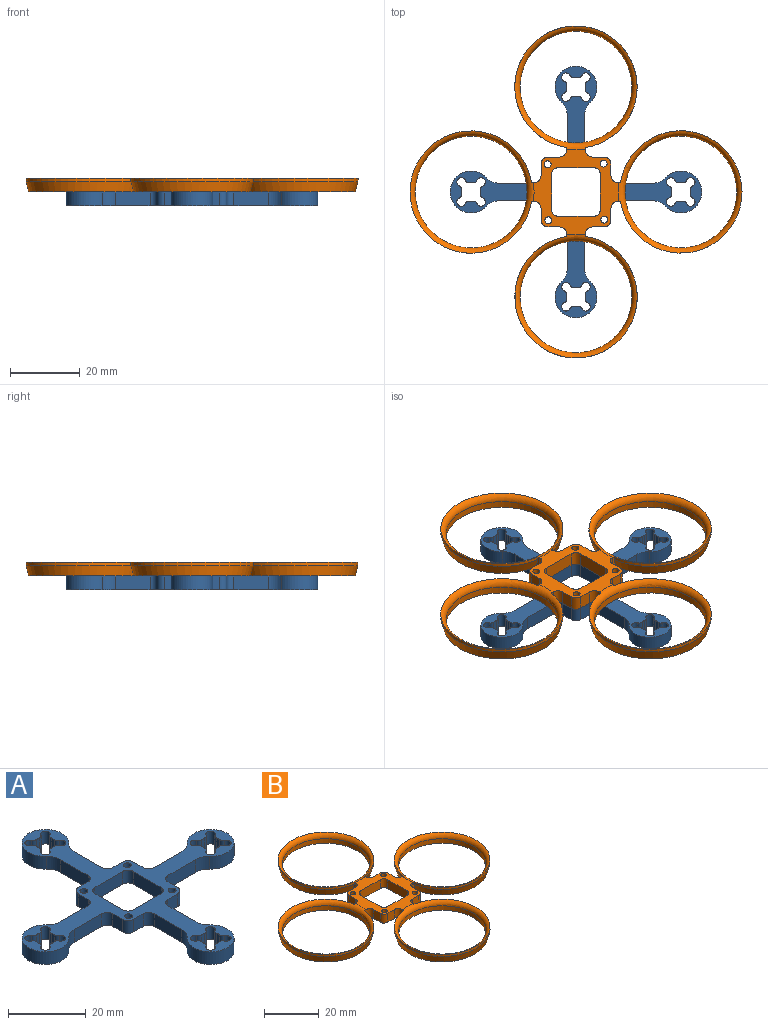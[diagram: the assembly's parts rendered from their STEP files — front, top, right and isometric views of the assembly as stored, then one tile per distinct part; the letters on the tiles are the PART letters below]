
ASSEMBLY  parts=2 mates=1
PART A: 118 faces, bbox 72x72x4 mm
  f0: plane 9.95x4mm, normal (0,-1,0), area 39.8mm2, adj f13,f14,f39,f104
  f1: plane 9.95x4mm, normal (0,1,0), area 39.8mm2, adj f13,f14,f40,f105
  f2: plane 9.95x4mm, normal (1,0,0), area 39.8mm2, adj f13,f14,f58,f106
  f3: plane 9.95x4mm, normal (-1,0,0), area 39.8mm2, adj f13,f14,f59,f107
  f4: plane 9.95x4mm, normal (-1,0,0), area 39.8mm2, adj f13,f14,f19,f102
  f5: plane 9.95x4mm, normal (1,0,0), area 39.8mm2, adj f13,f14,f20,f103
  f6: cylinder r=6mm len=12mm, axis (0,0,-1), area 114.8mm2, adj f13,f14,f19,f20
  f7: cylinder r=1.25mm len=4mm, axis (0,0,-1), area 19.7mm2, adj f13,f14,f17,f24
  f8: cylinder r=2.75mm len=4mm, axis (0,0,-1), area 4.4mm2, adj f13,f14,f15,f17
  f9: cylinder r=1.25mm len=4mm, axis (0,0,-1), area 19.7mm2, adj f13,f14,f15,f26
  f10: cylinder r=1.25mm len=4mm, axis (0,0,-1), area 19.7mm2, adj f13,f14,f16,f25
  f11: cylinder r=2.75mm len=4mm, axis (0,0,-1), area 4.4mm2, adj f13,f14,f16,f18
  f12: cylinder r=1.25mm len=4mm, axis (0,0,-1), area 19.7mm2, adj f13,f14,f18,f23
  f13: plane 72x72mm, normal (0,0,1), area 757.1mm2, adj f0,f1,f2,f3,f4,f5,f6,f7
  f14: plane 72x72mm, normal (0,0,-1), area 757.1mm2, adj f0,f1,f2,f3,f4,f5,f6,f7
  f15: cylinder r=1mm len=4mm, axis (0,0,-1), area 5.5mm2, adj f8,f9,f13,f14
  f16: cylinder r=1mm len=4mm, axis (0,0,-1), area 5.5mm2, adj f10,f11,f13,f14
  f17: cylinder r=1mm len=4mm, axis (0,0,-1), area 5.5mm2, adj f7,f8,f13,f14
  f18: cylinder r=1mm len=4mm, axis (0,0,-1), area 5.5mm2, adj f11,f12,f13,f14
  f19: cylinder r=5mm len=4mm, axis (0,0,-1), area 16.4mm2, adj f4,f6,f13,f14
  f20: cylinder r=5mm len=4mm, axis (0,0,-1), area 16.4mm2, adj f5,f6,f13,f14
  f21: cylinder r=2.75mm len=4mm, axis (0,0,-1), area 4.4mm2, adj f13,f14,f23,f24
  f22: cylinder r=2.75mm len=4mm, axis (0,0,-1), area 4.4mm2, adj f13,f14,f25,f26
  f23: cylinder r=1mm len=4mm, axis (0,0,-1), area 5.5mm2, adj f12,f13,f14,f21
  f24: cylinder r=1mm len=4mm, axis (0,0,-1), area 5.5mm2, adj f7,f13,f14,f21
  f25: cylinder r=1mm len=4mm, axis (0,0,-1), area 5.5mm2, adj f10,f13,f14,f22
  f26: cylinder r=1mm len=4mm, axis (0,0,-1), area 5.5mm2, adj f9,f13,f14,f22
  f27: plane 9.95x4mm, normal (0,1,0), area 39.8mm2, adj f13,f14,f78,f108
  f28: cylinder r=6mm len=12mm, axis (0,0,-1), area 114.8mm2, adj f13,f14,f39,f40
  f29: cylinder r=1.25mm len=4mm, axis (0,0,-1), area 19.7mm2, adj f13,f14,f37,f44
  f30: cylinder r=2.75mm len=4mm, axis (0,0,-1), area 4.4mm2, adj f13,f14,f35,f37
  f31: cylinder r=1.25mm len=4mm, axis (0,0,-1), area 19.7mm2, adj f13,f14,f35,f46
  f32: cylinder r=1.25mm len=4mm, axis (0,0,-1), area 19.7mm2, adj f13,f14,f36,f45
  f33: cylinder r=2.75mm len=4mm, axis (0,0,-1), area 4.4mm2, adj f13,f14,f36,f38
  f34: cylinder r=1.25mm len=4mm, axis (0,0,-1), area 19.7mm2, adj f13,f14,f38,f43
  f35: cylinder r=1mm len=4mm, axis (0,0,-1), area 5.5mm2, adj f13,f14,f30,f31
  f36: cylinder r=1mm len=4mm, axis (0,0,-1), area 5.5mm2, adj f13,f14,f32,f33
  f37: cylinder r=1mm len=4mm, axis (0,0,-1), area 5.5mm2, adj f13,f14,f29,f30
  f38: cylinder r=1mm len=4mm, axis (0,0,-1), area 5.5mm2, adj f13,f14,f33,f34
  f39: cylinder r=5mm len=4mm, axis (0,0,-1), area 16.4mm2, adj f0,f13,f14,f28
  f40: cylinder r=5mm len=4mm, axis (0,0,-1), area 16.4mm2, adj f1,f13,f14,f28
  f41: cylinder r=2.75mm len=4mm, axis (0,0,-1), area 4.4mm2, adj f13,f14,f43,f44
  f42: cylinder r=2.75mm len=4mm, axis (0,0,-1), area 4.4mm2, adj f13,f14,f45,f46
  f43: cylinder r=1mm len=4mm, axis (0,0,-1), area 5.5mm2, adj f13,f14,f34,f41
  f44: cylinder r=1mm len=4mm, axis (0,0,-1), area 5.5mm2, adj f13,f14,f29,f41
  f45: cylinder r=1mm len=4mm, axis (0,0,-1), area 5.5mm2, adj f13,f14,f32,f42
  f46: cylinder r=1mm len=4mm, axis (0,0,-1), area 5.5mm2, adj f13,f14,f31,f42
  f47: cylinder r=6mm len=12mm, axis (0,0,-1), area 114.8mm2, adj f13,f14,f58,f59
  f48: cylinder r=1.25mm len=4mm, axis (0,0,-1), area 19.7mm2, adj f13,f14,f56,f63
  f49: cylinder r=2.75mm len=4mm, axis (0,0,-1), area 4.4mm2, adj f13,f14,f54,f56
  f50: cylinder r=1.25mm len=4mm, axis (0,0,-1), area 19.7mm2, adj f13,f14,f54,f65
  f51: cylinder r=1.25mm len=4mm, axis (0,0,-1), area 19.7mm2, adj f13,f14,f55,f64
  f52: cylinder r=2.75mm len=4mm, axis (0,0,-1), area 4.4mm2, adj f13,f14,f55,f57
  f53: cylinder r=1.25mm len=4mm, axis (0,0,-1), area 19.7mm2, adj f13,f14,f57,f62
  f54: cylinder r=1mm len=4mm, axis (0,0,-1), area 5.5mm2, adj f13,f14,f49,f50
  f55: cylinder r=1mm len=4mm, axis (0,0,-1), area 5.5mm2, adj f13,f14,f51,f52
  f56: cylinder r=1mm len=4mm, axis (0,0,-1), area 5.5mm2, adj f13,f14,f48,f49
  f57: cylinder r=1mm len=4mm, axis (0,0,-1), area 5.5mm2, adj f13,f14,f52,f53
  f58: cylinder r=5mm len=4mm, axis (0,0,-1), area 16.4mm2, adj f2,f13,f14,f47
  f59: cylinder r=5mm len=4mm, axis (0,0,-1), area 16.4mm2, adj f3,f13,f14,f47
  f60: cylinder r=2.75mm len=4mm, axis (0,0,-1), area 4.4mm2, adj f13,f14,f62,f63
  f61: cylinder r=2.75mm len=4mm, axis (0,0,-1), area 4.4mm2, adj f13,f14,f64,f65
  f62: cylinder r=1mm len=4mm, axis (0,0,-1), area 5.5mm2, adj f13,f14,f53,f60
  f63: cylinder r=1mm len=4mm, axis (0,0,-1), area 5.5mm2, adj f13,f14,f48,f60
  f64: cylinder r=1mm len=4mm, axis (0,0,-1), area 5.5mm2, adj f13,f14,f51,f61
  f65: cylinder r=1mm len=4mm, axis (0,0,-1), area 5.5mm2, adj f13,f14,f50,f61
  f66: cylinder r=6mm len=12mm, axis (0,0,-1), area 114.8mm2, adj f13,f14,f78,f79
  f67: cylinder r=1.25mm len=4mm, axis (0,0,-1), area 19.7mm2, adj f13,f14,f76,f83
  f68: cylinder r=2.75mm len=4mm, axis (0,0,-1), area 4.4mm2, adj f13,f14,f74,f76
  f69: cylinder r=1.25mm len=4mm, axis (0,0,-1), area 19.7mm2, adj f13,f14,f74,f85
  f70: cylinder r=1.25mm len=4mm, axis (0,0,-1), area 19.7mm2, adj f13,f14,f75,f84
  f71: cylinder r=2.75mm len=4mm, axis (0,0,-1), area 4.4mm2, adj f13,f14,f75,f77
  f72: cylinder r=1.25mm len=4mm, axis (0,0,-1), area 19.7mm2, adj f13,f14,f77,f82
  f73: plane 9.95x4mm, normal (0,-1,0), area 39.8mm2, adj f13,f14,f79,f109
  f74: cylinder r=1mm len=4mm, axis (0,0,-1), area 5.5mm2, adj f13,f14,f68,f69
  f75: cylinder r=1mm len=4mm, axis (0,0,-1), area 5.5mm2, adj f13,f14,f70,f71
  f76: cylinder r=1mm len=4mm, axis (0,0,-1), area 5.5mm2, adj f13,f14,f67,f68
  f77: cylinder r=1mm len=4mm, axis (0,0,-1), area 5.5mm2, adj f13,f14,f71,f72
  f78: cylinder r=5mm len=4mm, axis (0,0,-1), area 16.4mm2, adj f13,f14,f27,f66
  f79: cylinder r=5mm len=4mm, axis (0,0,-1), area 16.4mm2, adj f13,f14,f66,f73
  f80: cylinder r=2.75mm len=4mm, axis (0,0,-1), area 4.4mm2, adj f13,f14,f82,f83
  f81: cylinder r=2.75mm len=4mm, axis (0,0,-1), area 4.4mm2, adj f13,f14,f84,f85
  f82: cylinder r=1mm len=4mm, axis (0,0,-1), area 5.5mm2, adj f13,f14,f72,f80
  f83: cylinder r=1mm len=4mm, axis (0,0,-1), area 5.5mm2, adj f13,f14,f67,f80
  f84: cylinder r=1mm len=4mm, axis (0,0,-1), area 5.5mm2, adj f13,f14,f70,f81
  f85: cylinder r=1mm len=4mm, axis (0,0,-1), area 5.5mm2, adj f13,f14,f69,f81
  f86: cylinder r=1mm len=4mm, axis (0,0,-1), area 25.1mm2, adj f13,f14
  f87: plane 4x3.5mm, normal (1,0,0), area 14mm2, adj f13,f14,f109,f115
  f88: plane 4x3.5mm, normal (0,-1,0), area 14mm2, adj f13,f14,f106,f115
  f89: cylinder r=1mm len=4mm, axis (0,0,-1), area 25.1mm2, adj f13,f14
  f90: plane 4x3.5mm, normal (0,-1,0), area 14mm2, adj f13,f14,f107,f114
  f91: plane 4x3.5mm, normal (-1,0,0), area 14mm2, adj f13,f14,f104,f114
  f92: plane 10x4mm, normal (0,1,0), area 40mm2, adj f13,f14,f110,f111
  f93: cylinder r=1mm len=4mm, axis (0,0,-1), area 25.1mm2, adj f13,f14
  f94: plane 4x3.5mm, normal (-1,0,0), area 14mm2, adj f13,f14,f105,f113
  f95: plane 4x3.5mm, normal (0,1,0), area 14mm2, adj f13,f14,f102,f113
  f96: plane 10x4mm, normal (1,0,0), area 40mm2, adj f13,f14,f111,f112
  f97: plane 10x4mm, normal (0,-1,0), area 40mm2, adj f13,f14,f112,f116
  f98: plane 4x3.5mm, normal (0,1,0), area 14mm2, adj f13,f14,f103,f117
  f99: plane 10x4mm, normal (-1,0,0), area 40mm2, adj f13,f14,f110,f116
  f100: plane 4x3.5mm, normal (1,0,0), area 14mm2, adj f13,f14,f108,f117
  f101: cylinder r=1mm len=4mm, axis (0,0,-1), area 25.1mm2, adj f13,f14
  f102: cylinder r=2mm len=4mm, axis (0,0,1), area 12.6mm2, adj f4,f13,f14,f95
  f103: cylinder r=2mm len=4mm, axis (0,0,-1), area 12.6mm2, adj f5,f13,f14,f98
  f104: cylinder r=2mm len=4mm, axis (0,0,1), area 12.6mm2, adj f0,f13,f14,f91
  f105: cylinder r=2mm len=4mm, axis (0,0,-1), area 12.6mm2, adj f1,f13,f14,f94
  f106: cylinder r=2mm len=4mm, axis (0,0,1), area 12.6mm2, adj f2,f13,f14,f88
  f107: cylinder r=2mm len=4mm, axis (0,0,-1), area 12.6mm2, adj f3,f13,f14,f90
  f108: cylinder r=2mm len=4mm, axis (0,0,1), area 12.6mm2, adj f13,f14,f27,f100
  f109: cylinder r=2mm len=4mm, axis (0,0,-1), area 12.6mm2, adj f13,f14,f73,f87
  f110: cylinder r=2mm len=4mm, axis (0,0,-1), area 12.6mm2, adj f13,f14,f92,f99
  f111: cylinder r=2mm len=4mm, axis (0,0,1), area 12.6mm2, adj f13,f14,f92,f96
  f112: cylinder r=2mm len=4mm, axis (0,0,-1), area 12.6mm2, adj f13,f14,f96,f97
  f113: cylinder r=2mm len=4mm, axis (0,0,1), area 12.6mm2, adj f13,f14,f94,f95
  f114: cylinder r=2mm len=4mm, axis (0,0,-1), area 12.6mm2, adj f13,f14,f90,f91
  f115: cylinder r=2mm len=4mm, axis (0,0,1), area 12.6mm2, adj f13,f14,f87,f88
  f116: cylinder r=2mm len=4mm, axis (0,0,1), area 12.6mm2, adj f13,f14,f97,f99
  f117: cylinder r=2mm len=4mm, axis (0,0,-1), area 12.6mm2, adj f13,f14,f98,f100
PART B: 58 faces, bbox 102.1x99x4 mm
  f0: plane 10x4mm, normal (0,-1,0), area 40mm2, adj f32,f33,f46,f49
  f1: plane 10x4mm, normal (-1,0,0), area 40mm2, adj f32,f33,f46,f47
  f2: plane 10x4mm, normal (0,1,0), area 40mm2, adj f32,f33,f47,f48
  f3: cylinder r=17.5mm len=35mm, axis (0,0,-1), area 97.9mm2, adj f4,f30,f50,f57
  f4: plane 4x1.53mm, normal (-1,0,0), area 4mm2, adj f3,f32,f33,f34,f50,f57
  f5: plane 4x3.31mm, normal (0,1,0), area 13.2mm2, adj f32,f33,f34,f36
  f6: plane 4x3.33mm, normal (-1,0,0), area 13.3mm2, adj f32,f33,f36,f37
  f7: plane 4x1.53mm, normal (0,1,0), area 4mm2, adj f8,f32,f33,f37,f51,f56
  f8: cylinder r=17.5mm len=35mm, axis (0,0,-1), area 97.9mm2, adj f7,f9,f51,f56
  f9: plane 4x1.53mm, normal (0,-1,0), area 4mm2, adj f8,f32,f33,f38,f51,f56
  f10: plane 4x3.29mm, normal (-1,0,0), area 13.2mm2, adj f32,f33,f38,f39
  f11: plane 4x3.34mm, normal (0,-1,0), area 13.4mm2, adj f32,f33,f39,f40
  f12: plane 4x1.53mm, normal (-1,0,0), area 4.1mm2, adj f13,f32,f33,f40,f52,f55
  f13: cylinder r=17.5mm len=35mm, axis (0,0,-1), area 97.9mm2, adj f12,f14,f52,f55
  f14: plane 4x1.53mm, normal (1,0,0), area 4.1mm2, adj f13,f32,f33,f41,f52,f55
  f15: plane 4x3.3mm, normal (0,-1,0), area 13.2mm2, adj f32,f33,f41,f42
  f16: plane 4x3.33mm, normal (1,0,0), area 13.3mm2, adj f32,f33,f42,f43
  f17: plane 4x1.53mm, normal (0,-1,0), area 4.1mm2, adj f18,f32,f33,f43,f53,f54
  f18: cylinder r=17.5mm len=35mm, axis (0,0,-1), area 97.9mm2, adj f17,f19,f53,f54
  f19: plane 4x1.53mm, normal (0,1,0), area 4.1mm2, adj f18,f32,f33,f44,f53,f54
  f20: plane 4x3.32mm, normal (1,0,0), area 13.3mm2, adj f32,f33,f44,f45
  f21: plane 4x3.31mm, normal (0,1,0), area 13.3mm2, adj f32,f33,f35,f45
  f22: cylinder r=16mm len=32mm, axis (0,0,-1), area 201.1mm2, adj f33,f53
  f23: cylinder r=1mm len=4mm, axis (0,0,-1), area 25.1mm2, adj f32,f33
  f24: cylinder r=1mm len=4mm, axis (0,0,-1), area 25.1mm2, adj f32,f33
  f25: cylinder r=1mm len=4mm, axis (0,0,-1), area 25.1mm2, adj f32,f33
  f26: cylinder r=1mm len=4mm, axis (0,0,-1), area 25.1mm2, adj f32,f33
  f27: plane 10x4mm, normal (1,0,0), area 40mm2, adj f32,f33,f48,f49
  f28: cylinder r=16mm len=32mm, axis (0,0,-1), area 201.1mm2, adj f33,f51
  f29: cylinder r=16mm len=32mm, axis (0,0,-1), area 201.1mm2, adj f33,f50
  f30: plane 4x1.53mm, normal (1,0,0), area 4mm2, adj f3,f32,f33,f35,f50,f57
  f31: cylinder r=16mm len=32mm, axis (0,0,-1), area 201.1mm2, adj f33,f52
  f32: plane 24.43x24.43mm, normal (0,0,1), area 243.4mm2, adj f0,f1,f2,f4,f5,f6,f7,f9
  f33: plane 93.41x93.41mm, normal (0,0,-1), area 557.6mm2, adj f0,f1,f2,f4,f5,f6,f7,f9
  f34: cylinder r=2mm len=4mm, axis (0,0,-1), area 12.6mm2, adj f4,f5,f32,f33
  f35: cylinder r=2mm len=4mm, axis (0,0,1), area 12.6mm2, adj f21,f30,f32,f33
  f36: cylinder r=2mm len=4mm, axis (0,0,-1), area 12.6mm2, adj f5,f6,f32,f33
  f37: cylinder r=2mm len=4mm, axis (0,0,1), area 12.6mm2, adj f6,f7,f32,f33
  f38: cylinder r=2mm len=4mm, axis (0,0,1), area 12.6mm2, adj f9,f10,f32,f33
  f39: cylinder r=2mm len=4mm, axis (0,0,-1), area 12.5mm2, adj f10,f11,f32,f33
  f40: cylinder r=2mm len=4mm, axis (0,0,-1), area 12.5mm2, adj f11,f12,f32,f33
  f41: cylinder r=2mm len=4mm, axis (0,0,1), area 12.5mm2, adj f14,f15,f32,f33
  f42: cylinder r=2mm len=4mm, axis (0,0,1), area 12.5mm2, adj f15,f16,f32,f33
  f43: cylinder r=2mm len=4mm, axis (0,0,1), area 12.5mm2, adj f16,f17,f32,f33
  f44: cylinder r=2mm len=4mm, axis (0,0,-1), area 12.5mm2, adj f19,f20,f32,f33
  f45: cylinder r=2mm len=4mm, axis (0,0,-1), area 12.5mm2, adj f20,f21,f32,f33
  f46: cylinder r=2mm len=4mm, axis (0,0,1), area 12.6mm2, adj f0,f1,f32,f33
  f47: cylinder r=2mm len=4mm, axis (0,0,-1), area 12.6mm2, adj f1,f2,f32,f33
  f48: cylinder r=2mm len=4mm, axis (0,0,1), area 12.6mm2, adj f2,f27,f32,f33
  f49: cylinder r=2mm len=4mm, axis (0,0,-1), area 12.6mm2, adj f0,f27,f32,f33
  f50: torus R=18mm, axis (0,0,1), area 276.5mm2, adj f3,f4,f29,f30,f32
  f51: torus R=18mm, axis (0,0,1), area 276.5mm2, adj f7,f8,f9,f28,f32
  f52: torus R=18mm, axis (0,0,1), area 276.5mm2, adj f12,f13,f14,f31,f32
  f53: torus R=18mm, axis (0,0,1), area 276.5mm2, adj f17,f18,f19,f22,f32
  f54: cone r=17.5mm half-angle=15deg, axis (0,0,1), area 316.9mm2, adj f17,f18,f19,f33
  f55: cone r=17.5mm half-angle=15deg, axis (0,0,1), area 316.9mm2, adj f12,f13,f14,f33
  f56: cone r=17.5mm half-angle=15deg, axis (0,0,1), area 316.9mm2, adj f7,f8,f9,f33
  f57: cone r=17.5mm half-angle=15deg, axis (0,0,1), area 316.9mm2, adj f3,f4,f30,f33
PLACE A t=(24.72,27.82,1.8)mm
PLACE B t=(108.6,87.5,5.8)mm
MATE fastened A.f93 <-> B.f26  axis (0,0,1) through (16.6,35.72,5.8)mm
